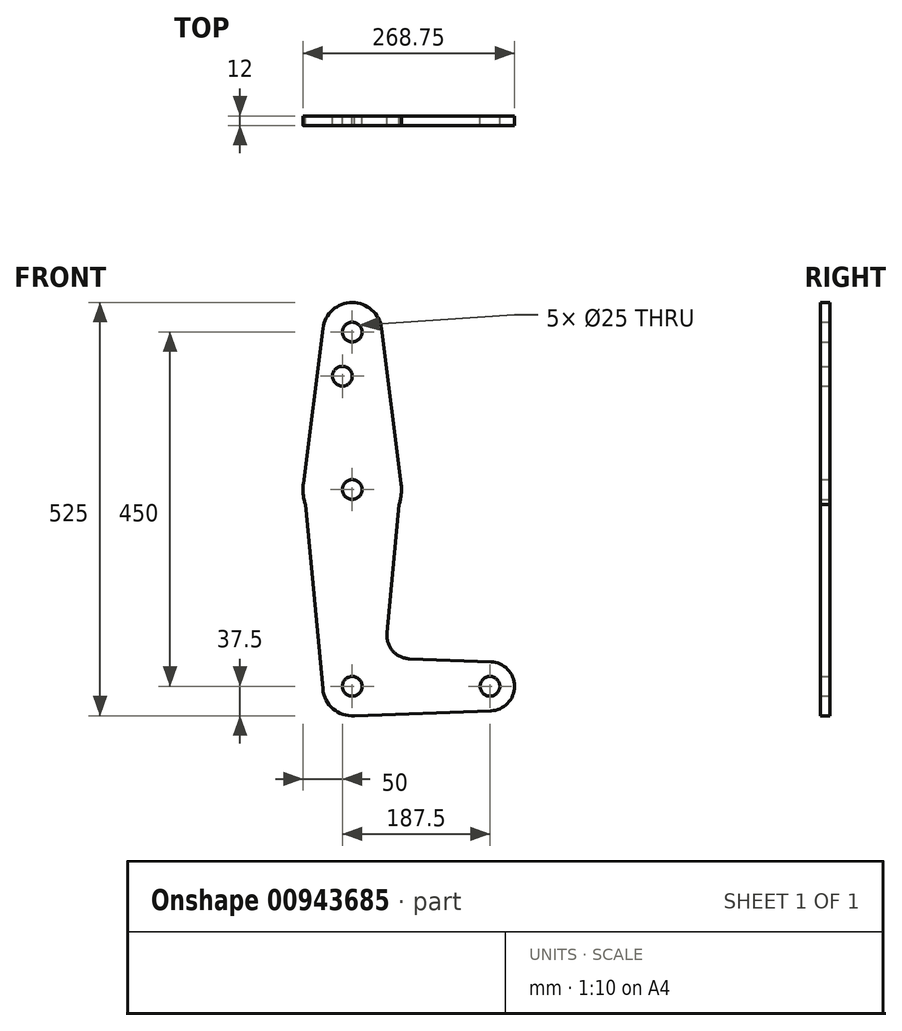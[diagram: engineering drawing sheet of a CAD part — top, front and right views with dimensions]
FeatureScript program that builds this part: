
annotation { "Feature Type Name" : "Feature", "Feature Type Description" : "" }
export const myFeature = defineFeature(function(context is Context, id is Id, definition is map)
    precondition{}
    {
        {
            var Q0;
            Q0=qCreatedBy(makeId("Front.planeOp"),FACE);
            var sketch = newSketch(context, id + "F0", { "sketchPlane" : qUnion([Q0])});
            skLineSegment(sketch, "E0", {"start": v(0, 0) * mm, "end": v(0, 450) * mm, "construction": true});
            skLineSegment(sketch, "E1", {"start": v(0, 0) * mm, "end": v(175, 0) * mm, "construction": true});
            skCircle(sketch, "E2", {"center": v(175, 0) * mm, "radius": 31.25 * mm});
            skCircle(sketch, "E3", {"center": v(0, 0) * mm, "radius": 37.5 * mm});
            skCircle(sketch, "E4", {"center": v(0, 250) * mm, "radius": 62.5 * mm});
            skCircle(sketch, "E5", {"center": v(0, 450) * mm, "radius": 37.5 * mm});
            skCircle(sketch, "E6", {"center": v(-12.5, 394) * mm, "radius": 12.5 * mm});
            skCircle(sketch, "E7", {"center": v(0, 450) * mm, "radius": 12.5 * mm});
            skCircle(sketch, "E8", {"center": v(0, 250) * mm, "radius": 12.5 * mm});
            skCircle(sketch, "E9", {"center": v(0, 0) * mm, "radius": 12.5 * mm});
            skCircle(sketch, "E10", {"center": v(175, 0) * mm, "radius": 12.5 * mm});
            skLineSegment(sketch, "E11", {"start": v(37.2, 454.69) * mm, "end": v(62, 257.81) * mm});
            skLineSegment(sketch, "E12", {"start": v(62, 257.81) * mm, "end": v(44.06, 67.7) * mm});
            skLineSegment(sketch, "E13", {"start": v(-37.2, 454.69) * mm, "end": v(-62, 257.81) * mm});
            skLineSegment(sketch, "E14", {"start": v(-62, 257.81) * mm, "end": v(-37.33, -3.53) * mm});
            skLineSegment(sketch, "E15", {"start": v(0, -37.5) * mm, "end": v(176.11, -31.23) * mm});
            skLineSegment(sketch, "E16", {"start": v(72.86, 34.9) * mm, "end": v(176.11, 31.23) * mm});
            skArc(sketch, "E17.filletArc", {"start": v(44.06, 67.7) * mm, "mid": v(51.38, 45.1) * mm, "end": v(72.86, 34.9) * mm});
            skSolve(sketch);
        }
        {
            var Q0;
            Q0 = qSketchRegion(id + "F0", true);
            extrude(context, id + "F1", {"entities" : qUnion([Q0]), "depth" : 12 * mm, "offsetDistance" : 25 * mm});
        }
    });
